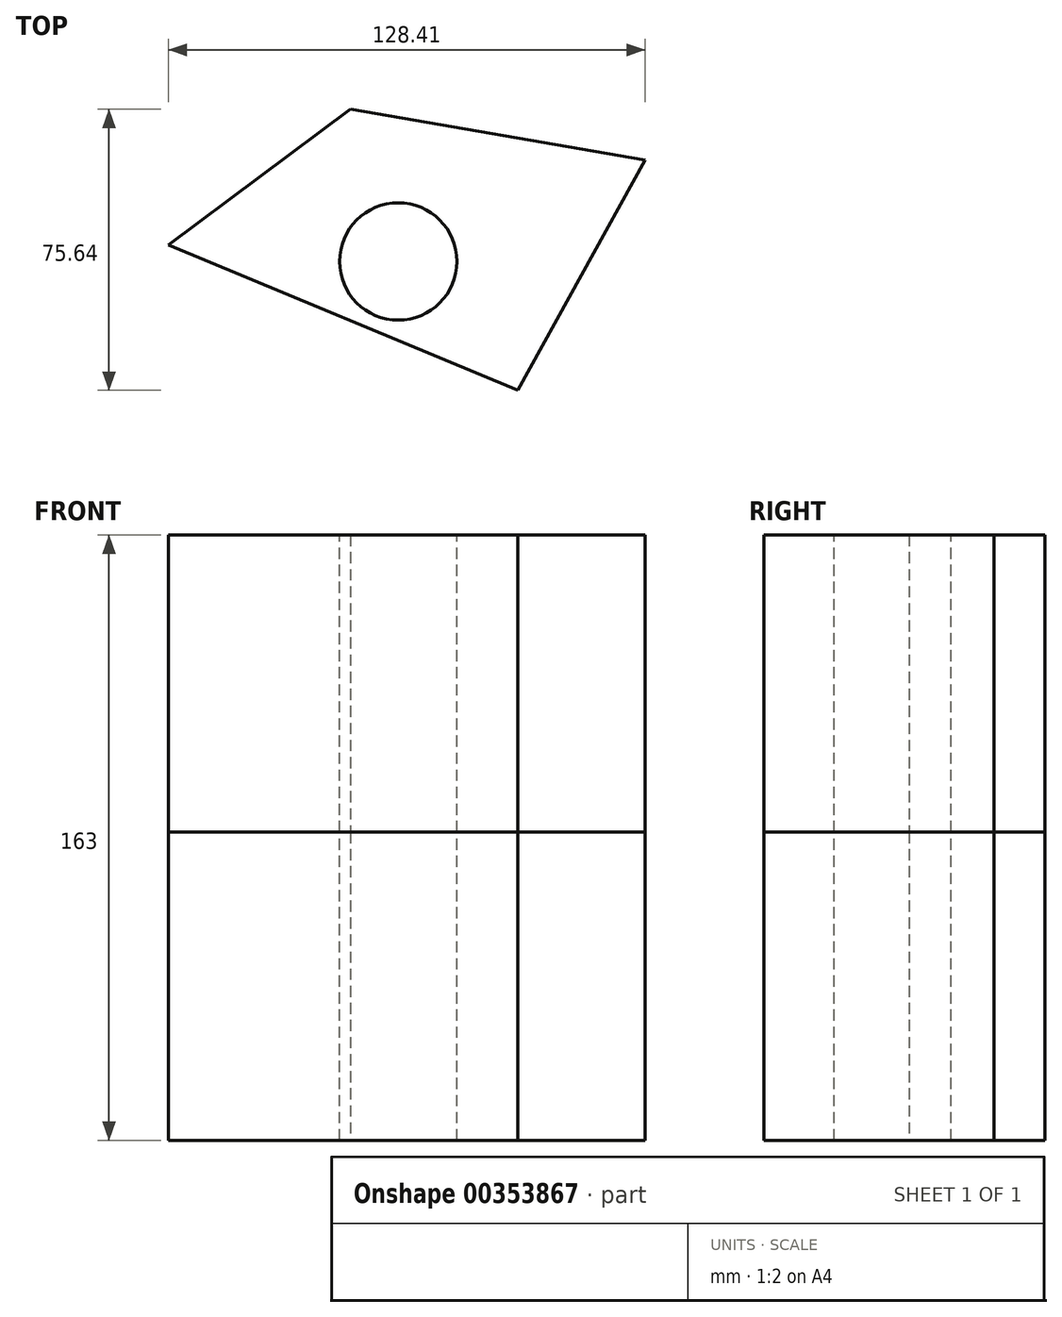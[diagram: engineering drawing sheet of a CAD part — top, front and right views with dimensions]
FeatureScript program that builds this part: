
annotation { "Feature Type Name" : "Feature", "Feature Type Description" : "" }
export const myFeature = defineFeature(function(context is Context, id is Id, definition is map)
    precondition{}
    {
        {
            var Q0;
            Q0=qCreatedBy(makeId("Top.planeOp"),FACE);
            var sketch = newSketch(context, id + "F0", { "sketchPlane" : qUnion([Q0])});
            skLineSegment(sketch, "E0", {"start": v(-69.74, 4.43) * mm, "end": v(-20.66, 40.96) * mm});
            skLineSegment(sketch, "E1", {"start": v(-20.66, 40.96) * mm, "end": v(58.67, 27.3) * mm});
            skLineSegment(sketch, "E2", {"start": v(58.67, 27.3) * mm, "end": v(24.35, -34.68) * mm});
            skLineSegment(sketch, "E3", {"start": v(-69.74, 4.43) * mm, "end": v(24.35, -34.68) * mm});
            skSolve(sketch);
        }
        {
            var Q0;
            Q0=makeQuery(id+"F0.imprint","IMPRINT",FACE,{"disambiguationData":[TD([[makeQuery(id+"F0.imprint","IMPRINT",EDGE,{"derivedFrom":sQuery(id+"F0.wireOp",EDGE,"E0")}),-1.0]])]});
            extrude(context, id + "F1", {"entities" : qUnion([Q0]), "depth" : 83 * mm});
        }
        {
            var Q0;
            Q0 = qSketchRegion(id + "F0", true);
            var Q1;
            Q1 = qConstructionFilter(qBodyType(qCreatedBy(id + "F0" ,EDGE), BodyType.WIRE), ConstructionObject.NO);
            extrude(context, id + "F2", {"entities" : qUnion([Q0]), "bodyType" : ToolBodyType.SURFACE, "surfaceEntities" : qUnion([Q1]), "depth" : 314 * mm});
        }
        {
            var Q0;
            Q0=makeQuery(id+"F1.opExtrude","CAP_FACE",FACE,{"disambiguationData":[OSD([sQuery(id+"F0.wireOp",EDGE,"E0"),sQuery(id+"F0.wireOp",EDGE,"E1"),sQuery(id+"F0.wireOp",EDGE,"E2"),sQuery(id+"F0.wireOp",EDGE,"E3")])],"isStart":false});
            extrude(context, id + "F3", {"entities" : qUnion([Q0]), "depth" : 80 * mm});
        }
        {
            var Q0;
            Q0=makeQuery(id+"F3.opExtrude","CAP_FACE",FACE,{"disambiguationData":[OSD([sQuery(id+"F0.wireOp",EDGE,"E0"),sQuery(id+"F0.wireOp",EDGE,"E1"),sQuery(id+"F0.wireOp",EDGE,"E2"),sQuery(id+"F0.wireOp",EDGE,"E3")])],"isStart":false});
            var sketch = newSketch(context, id + "F4", { "sketchPlane" : qUnion([Q0])});
            skCircle(sketch, "E4", {"center": v(-7.82, 0) * mm, "radius": 15.8 * mm});
            skSolve(sketch);
        }
        {
            var Q0;
            Q0 = qSketchRegion(id + "F4", true);
            extrude(context, id + "F5", {"entities" : qUnion([Q0]), "operationType" : NewBodyOperationType.REMOVE, "oppositeDirection" : true, "depth" : 261 * mm});
        }
    });
